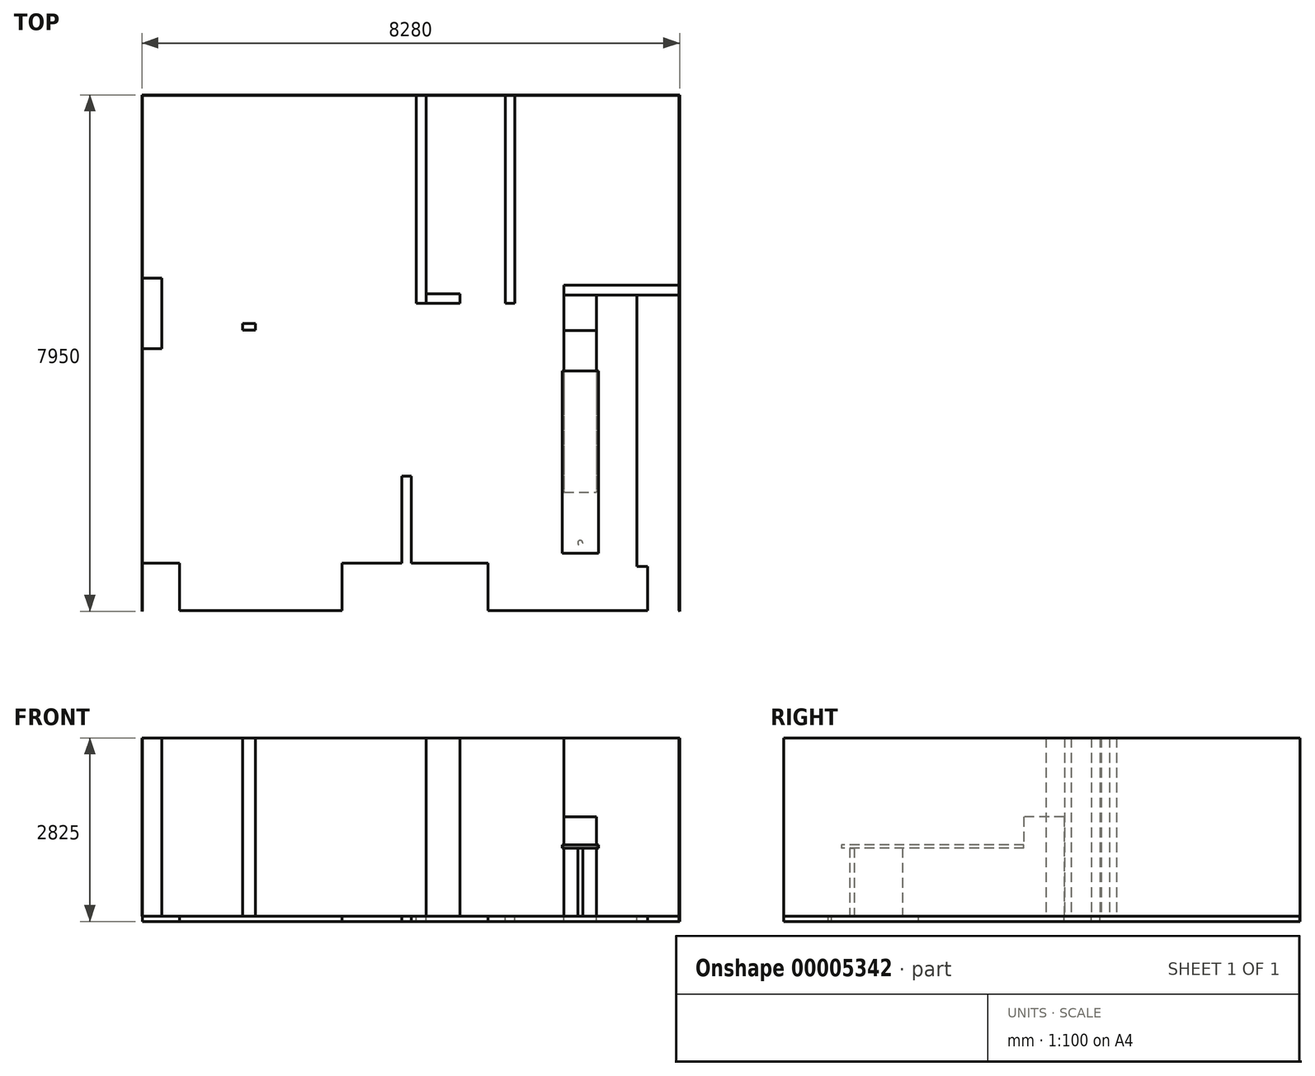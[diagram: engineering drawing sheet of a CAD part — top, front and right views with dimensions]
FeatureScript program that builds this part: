
annotation { "Feature Type Name" : "Feature", "Feature Type Description" : "" }
export const myFeature = defineFeature(function(context is Context, id is Id, definition is map)
    precondition{}
    {
        {
            var Q0;
            Q0=qCreatedBy(makeId("Top.planeOp"),FACE);
            var sketch = newSketch(context, id + "F0", { "sketchPlane" : qUnion([Q0])});
            skLineSegment(sketch, "E0.bottom", {"start": v(0, 0) * mm, "end": v(8260, 0) * mm});
            skLineSegment(sketch, "E0.top", {"start": v(0, 7930) * mm, "end": v(8260, 7930) * mm});
            skLineSegment(sketch, "E0.left", {"start": v(0, 0) * mm, "end": v(0, 7930) * mm});
            skLineSegment(sketch, "E0.right", {"start": v(8260, 0) * mm, "end": v(8260, 7930) * mm});
            skLineSegment(sketch, "E1.0", {"start": v(8270, -10) * mm, "end": v(8270, 7940) * mm});
            skLineSegment(sketch, "E1.1", {"start": v(-10, -10) * mm, "end": v(8270, -10) * mm});
            skLineSegment(sketch, "E1.2", {"start": v(-10, -10) * mm, "end": v(-10, 7940) * mm});
            skLineSegment(sketch, "E1.3", {"start": v(-10, 7940) * mm, "end": v(8270, 7940) * mm});
            skLineSegment(sketch, "E2.bottom", {"start": v(5585, 7930) * mm, "end": v(5735, 7930) * mm});
            skLineSegment(sketch, "E2.top", {"start": v(5585, 4730) * mm, "end": v(5735, 4730) * mm});
            skLineSegment(sketch, "E2.left", {"start": v(5585, 7930) * mm, "end": v(5585, 4730) * mm});
            skLineSegment(sketch, "E2.right", {"start": v(5735, 7930) * mm, "end": v(5735, 4730) * mm});
            skLineSegment(sketch, "E3.bottom", {"start": v(4215, 7930) * mm, "end": v(4365, 7930) * mm});
            skLineSegment(sketch, "E3.top", {"start": v(4215, 4730) * mm, "end": v(4365, 4730) * mm});
            skLineSegment(sketch, "E3.left", {"start": v(4215, 7930) * mm, "end": v(4215, 4730) * mm});
            skLineSegment(sketch, "E3.right", {"start": v(4365, 7930) * mm, "end": v(4365, 4730) * mm});
            skPoint(sketch, "E4", {"position": v(4290, 7930) * mm});
            skPoint(sketch, "E5", {"position": v(5660, 7930) * mm});
            skLineSegment(sketch, "E6.bottom", {"start": v(4365, 4730) * mm, "end": v(4885, 4730) * mm});
            skLineSegment(sketch, "E6.top", {"start": v(4365, 4880) * mm, "end": v(4885, 4880) * mm});
            skLineSegment(sketch, "E6.left", {"start": v(4365, 4730) * mm, "end": v(4365, 4880) * mm});
            skLineSegment(sketch, "E6.right", {"start": v(4885, 4730) * mm, "end": v(4885, 4880) * mm});
            skLineSegment(sketch, "E7.bottom", {"start": v(8260, 5010) * mm, "end": v(6490, 5010) * mm});
            skLineSegment(sketch, "E7.top", {"start": v(8260, 4860) * mm, "end": v(6490, 4860) * mm});
            skLineSegment(sketch, "E7.left", {"start": v(8260, 5010) * mm, "end": v(8260, 4860) * mm});
            skLineSegment(sketch, "E7.right", {"start": v(6490, 5010) * mm, "end": v(6490, 4860) * mm});
            skLineSegment(sketch, "E8.bottom", {"start": v(8260, 0) * mm, "end": v(7780, 0) * mm});
            skLineSegment(sketch, "E8.top", {"start": v(8260, 680.4) * mm, "end": v(7780, 680.4) * mm});
            skLineSegment(sketch, "E8.left", {"start": v(8260, 0) * mm, "end": v(8260, 680.4) * mm});
            skLineSegment(sketch, "E8.right", {"start": v(7780, 0) * mm, "end": v(7780, 680.4) * mm});
            skLineSegment(sketch, "E9.bottom", {"start": v(3070, 0) * mm, "end": v(5320, 0) * mm});
            skLineSegment(sketch, "E9.top", {"start": v(3070, 730) * mm, "end": v(5320, 730) * mm});
            skLineSegment(sketch, "E9.left", {"start": v(3070, 0) * mm, "end": v(3070, 730) * mm});
            skLineSegment(sketch, "E9.right", {"start": v(5320, 0) * mm, "end": v(5320, 730) * mm});
            skLineSegment(sketch, "E10.bottom", {"start": v(3990, 730) * mm, "end": v(4140, 730) * mm});
            skLineSegment(sketch, "E10.top", {"start": v(3990, 2070) * mm, "end": v(4140, 2070) * mm});
            skLineSegment(sketch, "E10.left", {"start": v(3990, 730) * mm, "end": v(3990, 2070) * mm});
            skLineSegment(sketch, "E10.right", {"start": v(4140, 730) * mm, "end": v(4140, 2070) * mm});
            skLineSegment(sketch, "E11.bottom", {"start": v(0, 0) * mm, "end": v(570, 0) * mm});
            skLineSegment(sketch, "E11.top", {"start": v(0, 730) * mm, "end": v(570, 730) * mm});
            skLineSegment(sketch, "E11.left", {"start": v(0, 0) * mm, "end": v(0, 730) * mm});
            skLineSegment(sketch, "E11.right", {"start": v(570, 0) * mm, "end": v(570, 730) * mm});
            skLineSegment(sketch, "E12.bottom", {"start": v(0, 4030) * mm, "end": v(300, 4030) * mm});
            skLineSegment(sketch, "E12.top", {"start": v(0, 5120) * mm, "end": v(300, 5120) * mm});
            skLineSegment(sketch, "E12.left", {"start": v(0, 4030) * mm, "end": v(0, 5120) * mm});
            skLineSegment(sketch, "E12.right", {"start": v(300, 4030) * mm, "end": v(300, 5120) * mm});
            skLineSegment(sketch, "E13.bottom", {"start": v(1540, 4420) * mm, "end": v(1740, 4420) * mm});
            skLineSegment(sketch, "E13.top", {"start": v(1540, 4320) * mm, "end": v(1740, 4320) * mm});
            skLineSegment(sketch, "E13.left", {"start": v(1540, 4420) * mm, "end": v(1540, 4320) * mm});
            skLineSegment(sketch, "E13.right", {"start": v(1740, 4420) * mm, "end": v(1740, 4320) * mm});
            skLineSegment(sketch, "E14.bottom", {"start": v(8260, 4860) * mm, "end": v(7610, 4860) * mm});
            skLineSegment(sketch, "E14.top", {"start": v(8260, 680.4) * mm, "end": v(7610, 680.4) * mm});
            skLineSegment(sketch, "E14.left", {"start": v(8260, 4860) * mm, "end": v(8260, 680.4) * mm});
            skLineSegment(sketch, "E14.right", {"start": v(7610, 4860) * mm, "end": v(7610, 680.4) * mm});
            skLineSegment(sketch, "E15.bottom", {"start": v(6490, 4860) * mm, "end": v(6990, 4860) * mm});
            skLineSegment(sketch, "E15.top", {"start": v(6490, 4310) * mm, "end": v(6990, 4310) * mm});
            skLineSegment(sketch, "E15.left", {"start": v(6490, 4860) * mm, "end": v(6490, 4310) * mm});
            skLineSegment(sketch, "E15.right", {"start": v(6990, 4860) * mm, "end": v(6990, 4310) * mm});
            skLineSegment(sketch, "E16.top", {"start": v(6490, 3690) * mm, "end": v(6990, 3690) * mm});
            skLineSegment(sketch, "E16.left", {"start": v(6490, 4310) * mm, "end": v(6490, 3690) * mm});
            skLineSegment(sketch, "E16.right", {"start": v(6990, 4310) * mm, "end": v(6990, 3690) * mm});
            skLineSegment(sketch, "E17.top", {"start": v(6490, 1823.43) * mm, "end": v(6990, 1823.43) * mm});
            skLineSegment(sketch, "E17.left", {"start": v(6490, 3690) * mm, "end": v(6490, 1823.43) * mm});
            skLineSegment(sketch, "E17.right", {"start": v(6990, 3690) * mm, "end": v(6990, 1823.43) * mm});
            skLineSegment(sketch, "E18.top", {"start": v(6490, 883.43) * mm, "end": v(6990, 883.43) * mm});
            skLineSegment(sketch, "E18.left", {"start": v(6490, 1823.43) * mm, "end": v(6490, 883.43) * mm});
            skLineSegment(sketch, "E18.right", {"start": v(6990, 1823.43) * mm, "end": v(6990, 883.43) * mm});
            skLineSegment(sketch, "E19", {"start": v(6740, 883.43) * mm, "end": v(6740, 1664.56) * mm, "construction": true});
            skCircle(sketch, "E20", {"center": v(6740, 1043.43) * mm, "radius": 37.5 * mm});
            skLineSegment(sketch, "E21", {"start": v(-10, 7940) * mm, "end": v(0, 7930) * mm});
            skLineSegment(sketch, "E22", {"start": v(8260, 7930) * mm, "end": v(8270, 7940) * mm});
            skLineSegment(sketch, "E23", {"start": v(8260, 0) * mm, "end": v(8270, -10) * mm});
            skLineSegment(sketch, "E24", {"start": v(-10, -10) * mm, "end": v(0, 0) * mm});
            skSolve(sketch);
        }
        {
            var Q0;
            Q0=makeQuery(id+"F0.imprint","IMPRINT",FACE,{"disambiguationData":[TD([[makeQuery(id+"F0.imprint","IMPRINT",EDGE,{"derivedFrom":sQuery(id+"F0.wireOp",EDGE,"E6.bottom")}),1.0]])]});
            var Q1;
            Q1=makeQuery(id+"F0.imprint","IMPRINT",FACE,{"disambiguationData":[TD([[makeQuery(id+"F0.imprint","IMPRINT",EDGE,{"derivedFrom":sQuery(id+"F0.wireOp",EDGE,"E2.top")}),-1.0]])]});
            var Q2;
            Q2=makeQuery(id+"F0.imprint","IMPRINT",FACE,{"disambiguationData":[TD([[makeQuery(id+"F0.imprint","IMPRINT",EDGE,{"derivedFrom":sQuery(id+"F0.wireOp",EDGE,"E8.bottom")}),-1.0]])]});
            var Q3;
            Q3=makeQuery(id+"F0.imprint","IMPRINT",FACE,{"disambiguationData":[TD([[makeQuery(id+"F0.imprint","IMPRINT",EDGE,{"derivedFrom":sQuery(id+"F0.wireOp",EDGE,"E9.bottom")}),1.0]])]});
            var Q4;
            Q4=makeQuery(id+"F0.imprint","IMPRINT",FACE,{"disambiguationData":[TD([[makeQuery(id+"F0.imprint","IMPRINT",EDGE,{"derivedFrom":sQuery(id+"F0.wireOp",EDGE,"E12.bottom")}),1.0]])]});
            var Q5;
            Q5=makeQuery(id+"F0.imprint","IMPRINT",FACE,{"disambiguationData":[TD([[makeQuery(id+"F0.imprint","IMPRINT",EDGE,{"derivedFrom":sQuery(id+"F0.wireOp",EDGE,"E11.bottom")}),1.0]])]});
            var Q6;
            Q6=makeQuery(id+"F0.imprint","IMPRINT",FACE,{"disambiguationData":[TD([[makeQuery(id+"F0.imprint","IMPRINT",EDGE,{"derivedFrom":sQuery(id+"F0.wireOp",EDGE,"E2.bottom")}),-1.0]])]});
            var Q7;
            Q7=makeQuery(id+"F0.imprint","IMPRINT",FACE,{"disambiguationData":[TD([[makeQuery(id+"F0.imprint","IMPRINT",EDGE,{"derivedFrom":sQuery(id+"F0.wireOp",EDGE,"E7.bottom")}),1.0]])]});
            var Q8;
            Q8=makeQuery(id+"F0.imprint","IMPRINT",FACE,{"disambiguationData":[TD([[makeQuery(id+"F0.imprint","IMPRINT",EDGE,{"derivedFrom":sQuery(id+"F0.wireOp",EDGE,"E1.0")}),1.0]])]});
            var Q9;
            Q9=makeQuery(id+"F0.imprint","IMPRINT",FACE,{"disambiguationData":[TD([[makeQuery(id+"F0.imprint","IMPRINT",EDGE,{"derivedFrom":sQuery(id+"F0.wireOp",EDGE,"E3.bottom")}),-1.0]])]});
            var Q10;
            Q10=makeQuery(id+"F0.imprint","IMPRINT",FACE,{"disambiguationData":[TD([[makeQuery(id+"F0.imprint","IMPRINT",EDGE,{"derivedFrom":sQuery(id+"F0.wireOp",EDGE,"E10.bottom")}),1.0]])]});
            var Q11;
            Q11=makeQuery(id+"F0.imprint","IMPRINT",FACE,{"disambiguationData":[TD([[makeQuery(id+"F0.imprint","IMPRINT",EDGE,{"derivedFrom":sQuery(id+"F0.wireOp",EDGE,"E13.bottom")}),-1.0]])]});
            var Q12;
            Q12=makeQuery(id+"F0.imprint","IMPRINT",FACE,{"disambiguationData":[TD([[makeQuery(id+"F0.imprint","IMPRINT",EDGE,{"derivedFrom":sQuery(id+"F0.wireOp",EDGE,"E15.bottom")}),-1.0]])]});
            var Q13;
            Q13=makeQuery(id+"F0.imprint","IMPRINT",FACE,{"disambiguationData":[TD([[makeQuery(id+"F0.imprint","IMPRINT",EDGE,{"derivedFrom":sQuery(id+"F0.wireOp",EDGE,"E15.top")}),-1.0]])]});
            var Q14;
            Q14=makeQuery(id+"F0.imprint","IMPRINT",FACE,{"disambiguationData":[TD([[makeQuery(id+"F0.imprint","IMPRINT",EDGE,{"derivedFrom":sQuery(id+"F0.wireOp",EDGE,"E16.top")}),-1.0]])]});
            var Q15;
            Q15=makeQuery(id+"F0.imprint","IMPRINT",FACE,{"disambiguationData":[TD([[makeQuery(id+"F0.imprint","IMPRINT",EDGE,{"derivedFrom":sQuery(id+"F0.wireOp",EDGE,"E17.top")}),-1.0]])]});
            var Q16;
            Q16=makeQuery(id+"F0.imprint","IMPRINT",FACE,{"disambiguationData":[TD([[makeQuery(id+"F0.imprint","IMPRINT",EDGE,{"derivedFrom":sQuery(id+"F0.wireOp",EDGE,"E14.bottom")}),1.0]])]});
            var Q17;
            Q17=makeQuery(id+"F0.imprint","IMPRINT",FACE,{"disambiguationData":[TD([[makeQuery(id+"F0.imprint","IMPRINT",EDGE,{"derivedFrom":sQuery(id+"F0.wireOp",EDGE,"E20")}),1.0]])]});
            extrude(context, id + "F1", {"entities" : qUnion([Q0, Q1, Q2, Q3, Q4, Q5, Q6, Q7, Q8, Q9, Q10, Q11, Q12, Q13, Q14, Q15, Q16, Q17]), "oppositeDirection" : true, "depth" : 80 * mm});
        }
        {
            var Q0;
            Q0=makeQuery(id+"F0.imprint","IMPRINT",FACE,{"disambiguationData":[TD([[makeQuery(id+"F0.imprint","IMPRINT",EDGE,{"derivedFrom":sQuery(id+"F0.wireOp",EDGE,"E1.0")}),1.0]])]});
            extrude(context, id + "F2", {"entities" : qUnion([Q0]), "depth" : 2745 * mm});
        }
        {
            var Q0;
            Q0=makeQuery(id+"F0.imprint","IMPRINT",FACE,{"disambiguationData":[TD([[makeQuery(id+"F0.imprint","IMPRINT",EDGE,{"derivedFrom":sQuery(id+"F0.wireOp",EDGE,"E12.bottom")}),1.0]])]});
            var Q1;
            Q1=makeQuery(id+"F0.imprint","IMPRINT",FACE,{"disambiguationData":[TD([[makeQuery(id+"F0.imprint","IMPRINT",EDGE,{"derivedFrom":sQuery(id+"F0.wireOp",EDGE,"E3.bottom")}),-1.0]])]});
            var Q2;
            Q2=makeQuery(id+"F0.imprint","IMPRINT",FACE,{"disambiguationData":[TD([[makeQuery(id+"F0.imprint","IMPRINT",EDGE,{"derivedFrom":sQuery(id+"F0.wireOp",EDGE,"E6.bottom")}),1.0]])]});
            var Q3;
            Q3=makeQuery(id+"F0.imprint","IMPRINT",FACE,{"disambiguationData":[TD([[makeQuery(id+"F0.imprint","IMPRINT",EDGE,{"derivedFrom":sQuery(id+"F0.wireOp",EDGE,"E2.bottom")}),-1.0]])]});
            var Q4;
            Q4=makeQuery(id+"F0.imprint","IMPRINT",FACE,{"disambiguationData":[TD([[makeQuery(id+"F0.imprint","IMPRINT",EDGE,{"derivedFrom":sQuery(id+"F0.wireOp",EDGE,"E7.bottom")}),1.0]])]});
            var Q5;
            Q5=makeQuery(id+"F0.imprint","IMPRINT",FACE,{"disambiguationData":[TD([[makeQuery(id+"F0.imprint","IMPRINT",EDGE,{"derivedFrom":sQuery(id+"F0.wireOp",EDGE,"E10.bottom")}),1.0]])]});
            var Q6;
            Q6=makeQuery(id+"F0.imprint","IMPRINT",FACE,{"disambiguationData":[TD([[makeQuery(id+"F0.imprint","IMPRINT",EDGE,{"derivedFrom":sQuery(id+"F0.wireOp",EDGE,"E13.bottom")}),-1.0]])]});
            var Q7;
            Q7=makeQuery(id+"F0.imprint","IMPRINT",FACE,{"disambiguationData":[TD([[makeQuery(id+"F0.imprint","IMPRINT",EDGE,{"derivedFrom":sQuery(id+"F0.wireOp",EDGE,"E15.bottom")}),-1.0]])]});
            extrude(context, id + "F3", {"entities" : qUnion([Q0, Q1, Q2, Q3, Q4, Q5, Q6, Q7]), "depth" : 2745 * mm});
        }
        {
            var Q0;
            Q0=makeQuery(id+"F0.imprint","IMPRINT",FACE,{"disambiguationData":[TD([[makeQuery(id+"F0.imprint","IMPRINT",EDGE,{"derivedFrom":sQuery(id+"F0.wireOp",EDGE,"E15.top")}),-1.0]])]});
            extrude(context, id + "F4", {"entities" : qUnion([Q0]), "operationType" : NewBodyOperationType.ADD, "depth" : 1530 * mm});
        }
        {
            var Q0;
            Q0=makeQuery(id+"F0.imprint","IMPRINT",FACE,{"disambiguationData":[TD([[makeQuery(id+"F0.imprint","IMPRINT",EDGE,{"derivedFrom":sQuery(id+"F0.wireOp",EDGE,"E16.top")}),-1.0]])]});
            extrude(context, id + "F5", {"entities" : qUnion([Q0]), "operationType" : NewBodyOperationType.ADD, "depth" : 1050 * mm});
        }
        {
            var Q0;
            Q0=makeQuery(id+"F5.opExtrude","CAP_FACE",FACE,{"disambiguationData":[OSD([sQuery(id+"F0.wireOp",EDGE,"E16.top"),sQuery(id+"F0.wireOp",EDGE,"E17.left"),sQuery(id+"F0.wireOp",EDGE,"E17.right"),sQuery(id+"F0.wireOp",EDGE,"E17.top")])],"isStart":false});
            var sketch = newSketch(context, id + "F6", { "sketchPlane" : qUnion([Q0])});
            skLineSegment(sketch, "E25.0", {"start": v(6490, 3690) * mm, "end": v(6490, 1823.43) * mm});
            skLineSegment(sketch, "E25.2", {"start": v(6490, 3690) * mm, "end": v(6990, 3690) * mm});
            skLineSegment(sketch, "E25.3", {"start": v(6990, 3690) * mm, "end": v(6990, 1823.43) * mm});
            skLineSegment(sketch, "E25.4", {"start": v(6490, 883.43) * mm, "end": v(6990, 883.43) * mm});
            skLineSegment(sketch, "E25.5", {"start": v(6490, 1823.43) * mm, "end": v(6490, 883.43) * mm});
            skLineSegment(sketch, "E25.6", {"start": v(6990, 1823.43) * mm, "end": v(6990, 883.43) * mm});
            skLineSegment(sketch, "E26", {"start": v(6460, 3690) * mm, "end": v(6460, 883.43) * mm});
            skLineSegment(sketch, "E27", {"start": v(7020, 3690) * mm, "end": v(7020, 883.43) * mm});
            skLineSegment(sketch, "E28", {"start": v(7020, 883.43) * mm, "end": v(6460, 883.43) * mm});
            skLineSegment(sketch, "E29", {"start": v(6460, 3690) * mm, "end": v(7020, 3690) * mm});
            skSolve(sketch);
        }
        {
            var Q0;
            Q0 = qSketchRegion(id + "F6", true);
            extrude(context, id + "F7", {"entities" : qUnion([Q0]), "depth" : 50 * mm});
        }
        {
            var Q0;
            Q0=makeQuery(id+"F0.imprint","IMPRINT",FACE,{"disambiguationData":[TD([[makeQuery(id+"F0.imprint","IMPRINT",EDGE,{"derivedFrom":sQuery(id+"F0.wireOp",EDGE,"E20")}),1.0]])]});
            extrude(context, id + "F8", {"entities" : qUnion([Q0]), "operationType" : NewBodyOperationType.ADD, "endBound" : BoundingType.UP_TO_NEXT, "depth" : 25 * mm});
        }
        {
            var Q0;
            Q0=makeQuery(id+"F0.imprint","IMPRINT",FACE,{"disambiguationData":[TD([[makeQuery(id+"F0.imprint","IMPRINT",EDGE,{"derivedFrom":sQuery(id+"F0.wireOp",EDGE,"E1.3")}),-1.0]])]});
            var Q1;
            Q1=makeQuery(id+"F0.imprint","IMPRINT",FACE,{"disambiguationData":[TD([[makeQuery(id+"F0.imprint","IMPRINT",EDGE,{"derivedFrom":sQuery(id+"F0.wireOp",EDGE,"E1.2")}),-1.0]])]});
            extrude(context, id + "F9", {"entities" : qUnion([Q0, Q1]), "depth" : 2745 * mm});
        }
    });
